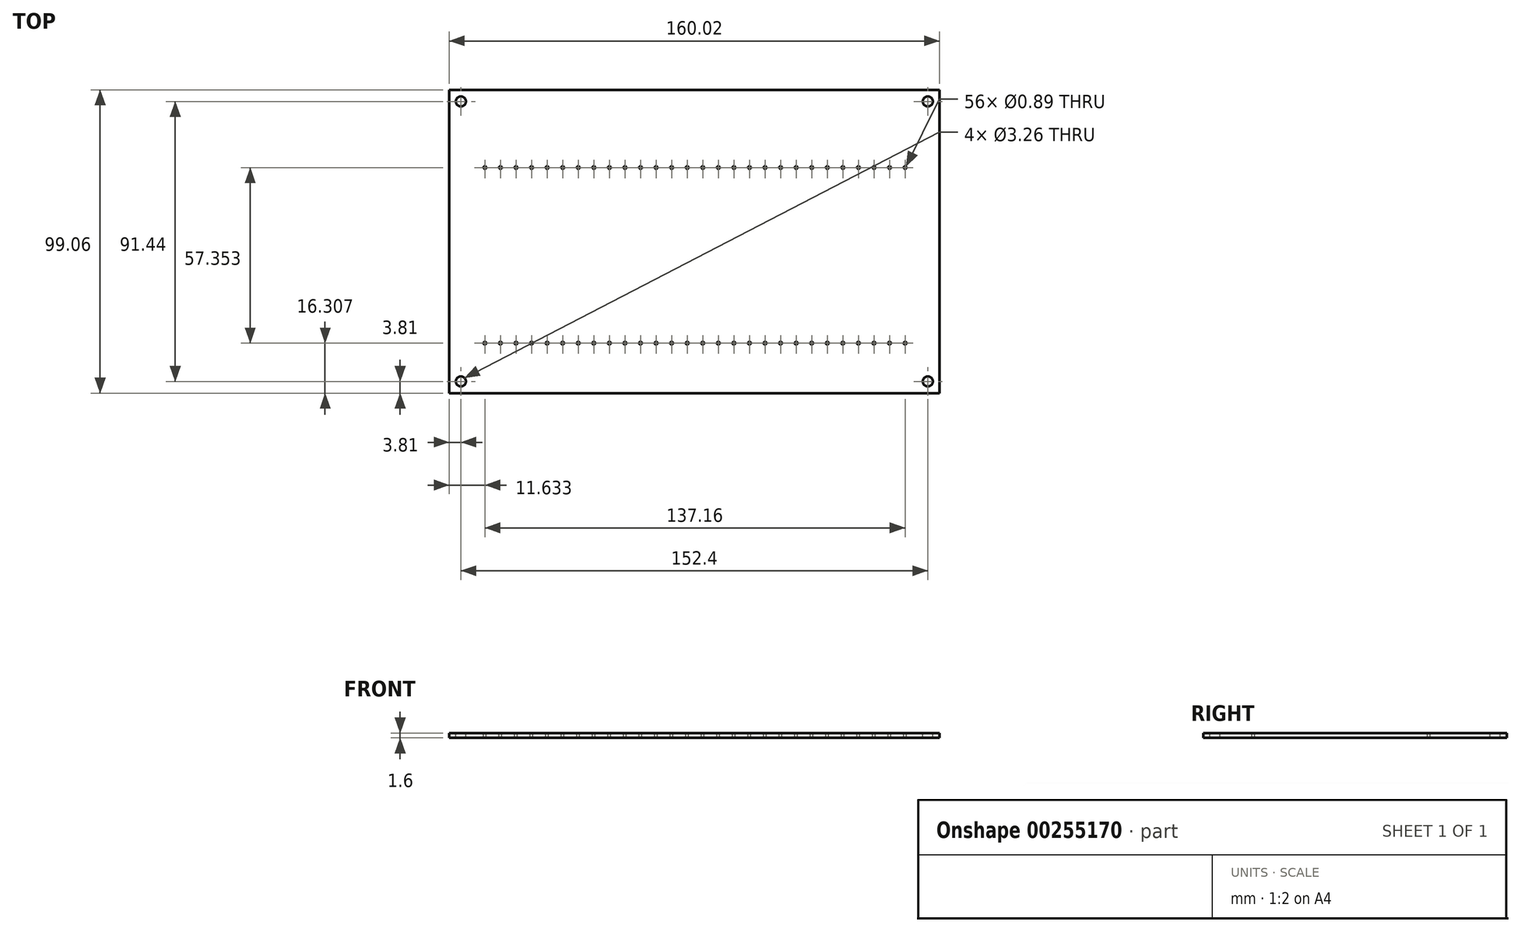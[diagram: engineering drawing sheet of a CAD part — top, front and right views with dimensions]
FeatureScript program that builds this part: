
annotation { "Feature Type Name" : "Feature", "Feature Type Description" : "" }
export const myFeature = defineFeature(function(context is Context, id is Id, definition is map)
    precondition{}
    {
        {
            var Q0;
            Q0=qCreatedBy(makeId("Top.planeOp"),FACE);
            var sketch = newSketch(context, id + "F0", { "sketchPlane" : qUnion([Q0])});
            skLineSegment(sketch, "E0.bottom", {"start": v(0, 0) * mm, "end": v(160.02, 0) * mm});
            skLineSegment(sketch, "E0.top", {"start": v(0, 99.06) * mm, "end": v(160.02, 99.06) * mm});
            skLineSegment(sketch, "E0.left", {"start": v(0, 0) * mm, "end": v(0, 99.06) * mm});
            skLineSegment(sketch, "E0.right", {"start": v(160.02, 0) * mm, "end": v(160.02, 99.06) * mm});
            skSolve(sketch);
        }
        {
            var Q0;
            Q0 = qSketchRegion(id + "F0", true);
            extrude(context, id + "F1", {"entities" : qUnion([Q0]), "depth" : 1.6 * mm});
        }
        {
            var Q0;
            Q0=makeQuery(id+"F1.opExtrude","CAP_FACE",FACE,{"disambiguationData":[OSD([sQuery(id+"F0.wireOp",EDGE,"E0.bottom"),sQuery(id+"F0.wireOp",EDGE,"E0.top"),sQuery(id+"F0.wireOp",EDGE,"E0.left"),sQuery(id+"F0.wireOp",EDGE,"E0.right")])],"isStart":false});
            var sketch = newSketch(context, id + "F2", { "sketchPlane" : qUnion([Q0])});
            skPoint(sketch, "E1", {"position": v(3.81, 3.81) * mm});
            skPoint(sketch, "E2", {"position": v(3.81, 95.25) * mm});
            skPoint(sketch, "E3", {"position": v(156.21, 95.25) * mm});
            skPoint(sketch, "E4", {"position": v(156.21, 3.81) * mm});
            skSolve(sketch);
        }
        {
            var Q0;
            Q0=sQuery(id+"F2.wireOp",VERTEX,"E2");
            var Q1;
            Q1=sQuery(id+"F2.wireOp",VERTEX,"E1");
            var Q2;
            Q2=sQuery(id+"F2.wireOp",VERTEX,"E4");
            var Q3;
            Q3=sQuery(id+"F2.wireOp",VERTEX,"E3");
            var Q4;
            Q4=makeQuery(id+"F1.opExtrude","SWEPT_BODY",BODY,{"disambiguationData":[OSD([sQuery(id+"F0.wireOp",EDGE,"E0.bottom"),sQuery(id+"F0.wireOp",EDGE,"E0.top"),sQuery(id+"F0.wireOp",EDGE,"E0.left"),sQuery(id+"F0.wireOp",EDGE,"E0.right")])]});
            hole(context, id + "F3", {"style" : HoleStyle.SIMPLE, "endStyle" : HoleEndStyle.THROUGH, "standardTappedOrClearance" : lookupTablePath({ "standard" : "ANSI", "fit" : "Normal (ASME)", "size" : "#4", "type" : "Clearance" }), "standardBlindInLast" : lookupTablePath({ "fit" : "Free", "standard" : "ANSI", "size" : "#4", "type" : "Clearance" }), "holeDiameter" : 3.26 * mm, "tappedDepth" : 2.77 * mm, "tapClearance" : 3, "startFromSketch" : true, "locations" : qUnion([Q0, Q1, Q2, Q3]), "scope" : qUnion([Q4])});
        }
        {
            var Q0;
            Q0=makeQuery(id+"F1.opExtrude","CAP_FACE",FACE,{"disambiguationData":[OSD([sQuery(id+"F0.wireOp",EDGE,"E0.bottom"),sQuery(id+"F0.wireOp",EDGE,"E0.top"),sQuery(id+"F0.wireOp",EDGE,"E0.left"),sQuery(id+"F0.wireOp",EDGE,"E0.right")])],"isStart":false});
            var sketch = newSketch(context, id + "F4", { "sketchPlane" : qUnion([Q0])});
            skPoint(sketch, "E5", {"position": v(11.63, 73.66) * mm});
            skPoint(sketch, "E6.1.0.0", {"position": v(16.71, 73.66) * mm});
            skPoint(sketch, "E6.2.0.0", {"position": v(21.8, 73.66) * mm});
            skPoint(sketch, "E6.3.0.0", {"position": v(26.87, 73.66) * mm});
            skPoint(sketch, "E6.4.0.0", {"position": v(31.95, 73.66) * mm});
            skPoint(sketch, "E6.5.0.0", {"position": v(37.03, 73.66) * mm});
            skPoint(sketch, "E6.6.0.0", {"position": v(42.11, 73.66) * mm});
            skPoint(sketch, "E6.7.0.0", {"position": v(47.2, 73.66) * mm});
            skPoint(sketch, "E6.8.0.0", {"position": v(52.27, 73.66) * mm});
            skPoint(sketch, "E6.9.0.0", {"position": v(57.35, 73.66) * mm});
            skPoint(sketch, "E6.10.0.0", {"position": v(62.43, 73.66) * mm});
            skPoint(sketch, "E6.11.0.0", {"position": v(67.51, 73.66) * mm});
            skPoint(sketch, "E6.12.0.0", {"position": v(72.6, 73.66) * mm});
            skPoint(sketch, "E6.13.0.0", {"position": v(77.67, 73.66) * mm});
            skPoint(sketch, "E6.14.0.0", {"position": v(82.75, 73.66) * mm});
            skPoint(sketch, "E6.15.0.0", {"position": v(87.83, 73.66) * mm});
            skPoint(sketch, "E6.16.0.0", {"position": v(92.91, 73.66) * mm});
            skPoint(sketch, "E6.17.0.0", {"position": v(98, 73.66) * mm});
            skPoint(sketch, "E6.18.0.0", {"position": v(103.07, 73.66) * mm});
            skPoint(sketch, "E6.19.0.0", {"position": v(108.15, 73.66) * mm});
            skPoint(sketch, "E6.20.0.0", {"position": v(113.23, 73.66) * mm});
            skPoint(sketch, "E6.21.0.0", {"position": v(118.31, 73.66) * mm});
            skPoint(sketch, "E6.22.0.0", {"position": v(123.4, 73.66) * mm});
            skPoint(sketch, "E6.23.0.0", {"position": v(128.47, 73.66) * mm});
            skPoint(sketch, "E6.24.0.0", {"position": v(133.55, 73.66) * mm});
            skPoint(sketch, "E6.25.0.0", {"position": v(138.63, 73.66) * mm});
            skPoint(sketch, "E6.26.0.0", {"position": v(143.71, 73.66) * mm});
            skPoint(sketch, "E6.27.0.0", {"position": v(148.8, 73.66) * mm});
            skLineSegment(sketch, "E6.direction1", {"start": v(11.63, 73.66) * mm, "end": v(16.71, 73.66) * mm, "construction": true});
            skSolve(sketch);
        }
        {
            var Q0;
            Q0=makeQuery(id+"F4.imprint","IMPRINT",FACE,{"disambiguationData":[TD([[makeQuery(id+"F4.imprint","IMPRINT",EDGE,{"derivedFrom":makeQuery(id+"F1.opExtrude","CAP_EDGE",EDGE,{"disambiguationData":[OSD([sQuery(id+"F0.wireOp",EDGE,"E0.bottom")])],"isStart":false})}),1.0]])]});
            var sketch = newSketch(context, id + "F5", { "sketchPlane" : qUnion([Q0])});
            skPoint(sketch, "E7", {"position": v(11.63, 16.3) * mm});
            skPoint(sketch, "E8.1.0.0", {"position": v(16.71, 16.3) * mm});
            skPoint(sketch, "E8.2.0.0", {"position": v(21.8, 16.3) * mm});
            skPoint(sketch, "E8.3.0.0", {"position": v(26.87, 16.3) * mm});
            skPoint(sketch, "E8.4.0.0", {"position": v(31.95, 16.3) * mm});
            skPoint(sketch, "E8.5.0.0", {"position": v(37.03, 16.3) * mm});
            skPoint(sketch, "E8.6.0.0", {"position": v(42.11, 16.3) * mm});
            skPoint(sketch, "E8.7.0.0", {"position": v(47.2, 16.3) * mm});
            skPoint(sketch, "E8.8.0.0", {"position": v(52.27, 16.3) * mm});
            skPoint(sketch, "E8.9.0.0", {"position": v(57.35, 16.3) * mm});
            skPoint(sketch, "E8.10.0.0", {"position": v(62.43, 16.3) * mm});
            skPoint(sketch, "E8.11.0.0", {"position": v(67.51, 16.3) * mm});
            skPoint(sketch, "E8.12.0.0", {"position": v(72.6, 16.3) * mm});
            skPoint(sketch, "E8.13.0.0", {"position": v(77.67, 16.3) * mm});
            skPoint(sketch, "E8.14.0.0", {"position": v(82.75, 16.3) * mm});
            skPoint(sketch, "E8.15.0.0", {"position": v(87.83, 16.3) * mm});
            skPoint(sketch, "E8.16.0.0", {"position": v(92.91, 16.3) * mm});
            skPoint(sketch, "E8.17.0.0", {"position": v(98, 16.3) * mm});
            skPoint(sketch, "E8.18.0.0", {"position": v(103.07, 16.3) * mm});
            skPoint(sketch, "E8.19.0.0", {"position": v(108.15, 16.3) * mm});
            skPoint(sketch, "E8.20.0.0", {"position": v(113.23, 16.3) * mm});
            skPoint(sketch, "E8.21.0.0", {"position": v(118.31, 16.3) * mm});
            skPoint(sketch, "E8.22.0.0", {"position": v(123.4, 16.3) * mm});
            skPoint(sketch, "E8.23.0.0", {"position": v(128.47, 16.3) * mm});
            skPoint(sketch, "E8.24.0.0", {"position": v(133.55, 16.3) * mm});
            skPoint(sketch, "E8.25.0.0", {"position": v(138.63, 16.3) * mm});
            skPoint(sketch, "E8.26.0.0", {"position": v(143.71, 16.3) * mm});
            skPoint(sketch, "E8.27.0.0", {"position": v(148.8, 16.3) * mm});
            skLineSegment(sketch, "E8.direction1", {"start": v(11.63, 16.3) * mm, "end": v(16.71, 16.3) * mm, "construction": true});
            skSolve(sketch);
        }
        {
            var Q0;
            Q0=sQuery(id+"F4.wireOp",VERTEX,"E6.15.0.0");
            var Q1;
            Q1=sQuery(id+"F4.wireOp",VERTEX,"E6.19.0.0");
            var Q2;
            Q2=sQuery(id+"F4.wireOp",VERTEX,"E6.22.0.0");
            var Q3;
            Q3=sQuery(id+"F4.wireOp",VERTEX,"E6.26.0.0");
            var Q4;
            Q4=sQuery(id+"F4.wireOp",VERTEX,"E6.14.0.0");
            var Q5;
            Q5=sQuery(id+"F4.wireOp",VERTEX,"E6.27.0.0");
            var Q6;
            Q6=sQuery(id+"F4.wireOp",VERTEX,"E6.18.0.0");
            var Q7;
            Q7=sQuery(id+"F4.wireOp",VERTEX,"E6.21.0.0");
            var Q8;
            Q8=sQuery(id+"F4.wireOp",VERTEX,"E6.25.0.0");
            var Q9;
            Q9=sQuery(id+"F4.wireOp",VERTEX,"E6.17.0.0");
            var Q10;
            Q10=sQuery(id+"F4.wireOp",VERTEX,"E6.24.0.0");
            var Q11;
            Q11=sQuery(id+"F4.wireOp",VERTEX,"E6.10.0.0");
            var Q12;
            Q12=sQuery(id+"F4.wireOp",VERTEX,"E6.9.0.0");
            var Q13;
            Q13=sQuery(id+"F4.wireOp",VERTEX,"E6.8.0.0");
            var Q14;
            Q14=sQuery(id+"F4.wireOp",VERTEX,"E6.7.0.0");
            var Q15;
            Q15=sQuery(id+"F4.wireOp",VERTEX,"E6.6.0.0");
            var Q16;
            Q16=sQuery(id+"F4.wireOp",VERTEX,"E6.5.0.0");
            var Q17;
            Q17=sQuery(id+"F4.wireOp",VERTEX,"E6.4.0.0");
            var Q18;
            Q18=sQuery(id+"F4.wireOp",VERTEX,"E6.3.0.0");
            var Q19;
            Q19=sQuery(id+"F4.wireOp",VERTEX,"E6.2.0.0");
            var Q20;
            Q20=sQuery(id+"F4.wireOp",VERTEX,"E6.1.0.0");
            var Q21;
            Q21=sQuery(id+"F4.wireOp",VERTEX,"E5");
            var Q22;
            Q22=sQuery(id+"F4.wireOp",VERTEX,"E6.13.0.0");
            var Q23;
            Q23=sQuery(id+"F4.wireOp",VERTEX,"E6.12.0.0");
            var Q24;
            Q24=sQuery(id+"F4.wireOp",VERTEX,"E6.11.0.0");
            var Q25;
            Q25=sQuery(id+"F4.wireOp",VERTEX,"E6.16.0.0");
            var Q26;
            Q26=sQuery(id+"F4.wireOp",VERTEX,"E6.20.0.0");
            var Q27;
            Q27=sQuery(id+"F4.wireOp",VERTEX,"E6.23.0.0");
            var Q28;
            Q28=sQuery(id+"F5.wireOp",VERTEX,"E8.20.0.0");
            var Q29;
            Q29=sQuery(id+"F5.wireOp",VERTEX,"E8.2.0.0");
            var Q30;
            Q30=sQuery(id+"F5.wireOp",VERTEX,"E8.22.0.0");
            var Q31;
            Q31=sQuery(id+"F5.wireOp",VERTEX,"E8.4.0.0");
            var Q32;
            Q32=sQuery(id+"F5.wireOp",VERTEX,"E8.3.0.0");
            var Q33;
            Q33=sQuery(id+"F5.wireOp",VERTEX,"E8.8.0.0");
            var Q34;
            Q34=sQuery(id+"F5.wireOp",VERTEX,"E8.1.0.0");
            var Q35;
            Q35=sQuery(id+"F5.wireOp",VERTEX,"E8.21.0.0");
            var Q36;
            Q36=sQuery(id+"F5.wireOp",VERTEX,"E8.5.0.0");
            var Q37;
            Q37=sQuery(id+"F5.wireOp",VERTEX,"E8.17.0.0");
            var Q38;
            Q38=sQuery(id+"F5.wireOp",VERTEX,"E8.7.0.0");
            var Q39;
            Q39=sQuery(id+"F5.wireOp",VERTEX,"E8.18.0.0");
            var Q40;
            Q40=sQuery(id+"F5.wireOp",VERTEX,"E8.27.0.0");
            var Q41;
            Q41=sQuery(id+"F5.wireOp",VERTEX,"E8.6.0.0");
            var Q42;
            Q42=sQuery(id+"F5.wireOp",VERTEX,"E8.19.0.0");
            var Q43;
            Q43=sQuery(id+"F5.wireOp",VERTEX,"E8.16.0.0");
            var Q44;
            Q44=sQuery(id+"F5.wireOp",VERTEX,"E8.9.0.0");
            var Q45;
            Q45=sQuery(id+"F5.wireOp",VERTEX,"E8.15.0.0");
            var Q46;
            Q46=sQuery(id+"F5.wireOp",VERTEX,"E8.10.0.0");
            var Q47;
            Q47=sQuery(id+"F5.wireOp",VERTEX,"E8.13.0.0");
            var Q48;
            Q48=sQuery(id+"F5.wireOp",VERTEX,"E8.12.0.0");
            var Q49;
            Q49=sQuery(id+"F5.wireOp",VERTEX,"E8.11.0.0");
            var Q50;
            Q50=sQuery(id+"F5.wireOp",VERTEX,"E8.14.0.0");
            var Q51;
            Q51=sQuery(id+"F5.wireOp",VERTEX,"E8.26.0.0");
            var Q52;
            Q52=sQuery(id+"F5.wireOp",VERTEX,"E8.25.0.0");
            var Q53;
            Q53=sQuery(id+"F5.wireOp",VERTEX,"E8.24.0.0");
            var Q54;
            Q54=sQuery(id+"F5.wireOp",VERTEX,"E7");
            var Q55;
            Q55=sQuery(id+"F5.wireOp",VERTEX,"E8.23.0.0");
            var Q56;
            Q56=makeQuery(id+"F1.opExtrude","SWEPT_BODY",BODY,{"disambiguationData":[OSD([sQuery(id+"F0.wireOp",EDGE,"E0.bottom"),sQuery(id+"F0.wireOp",EDGE,"E0.top"),sQuery(id+"F0.wireOp",EDGE,"E0.left"),sQuery(id+"F0.wireOp",EDGE,"E0.right")])]});
            hole(context, id + "F6", {"style" : HoleStyle.SIMPLE, "endStyle" : HoleEndStyle.THROUGH, "holeDiameter" : 0.89 * mm, "tappedDepth" : 2.77 * mm, "tapClearance" : 3, "startFromSketch" : true, "locations" : qUnion([Q0, Q1, Q2, Q3, Q4, Q5, Q6, Q7, Q8, Q9, Q10, Q11, Q12, Q13, Q14, Q15, Q16, Q17, Q18, Q19, Q20, Q21, Q22, Q23, Q24, Q25, Q26, Q27, Q28, Q29, Q30, Q31, Q32, Q33, Q34, Q35, Q36, Q37, Q38, Q39, Q40, Q41, Q42, Q43, Q44, Q45, Q46, Q47, Q48, Q49, Q50, Q51, Q52, Q53, Q54, Q55]), "scope" : qUnion([Q56])});
        }
    });
